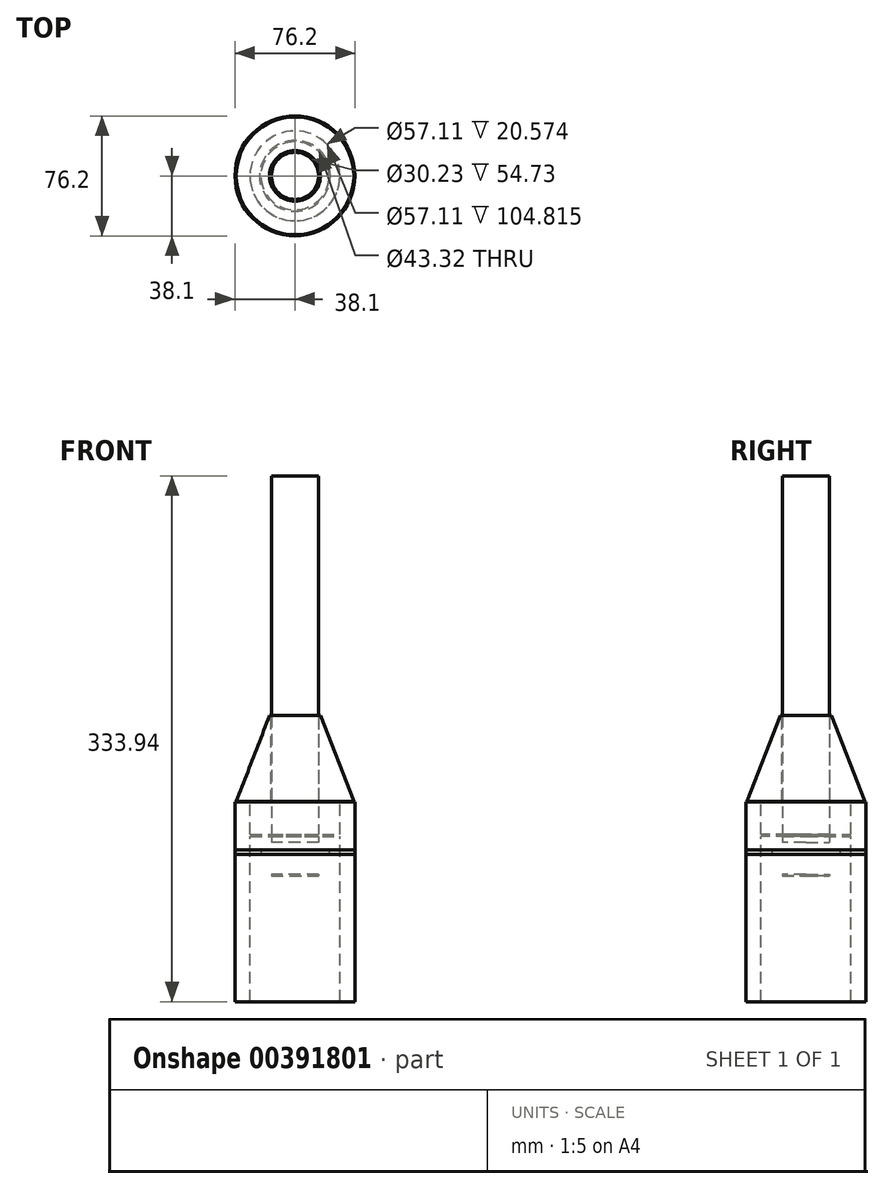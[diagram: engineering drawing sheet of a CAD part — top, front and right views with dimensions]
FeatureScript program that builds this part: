
annotation { "Feature Type Name" : "Feature", "Feature Type Description" : "" }
export const myFeature = defineFeature(function(context is Context, id is Id, definition is map)
    precondition{}
    {
        {
            var Q0;
            Q0=qCreatedBy(makeId("Front.planeOp"),FACE);
            var sketch = newSketch(context, id + "F0", { "sketchPlane" : qUnion([Q0])});
            skLineSegment(sketch, "E0.bottom", {"start": v(0, 67.99) * mm, "end": v(-38.1, 67.99) * mm});
            skLineSegment(sketch, "E0.top", {"start": v(0, -59.01) * mm, "end": v(-38.1, -59.01) * mm});
            skLineSegment(sketch, "E0.left", {"start": v(0, 67.99) * mm, "end": v(0, -59.01) * mm});
            skLineSegment(sketch, "E0.right", {"start": v(-38.1, 67.99) * mm, "end": v(-38.1, -59.01) * mm});
            skSolve(sketch);
        }
        {
            var Q0;
            Q0=makeQuery(id+"F0.imprint","IMPRINT",FACE,{"disambiguationData":[TD([[makeQuery(id+"F0.imprint","IMPRINT",EDGE,{"derivedFrom":sQuery(id+"F0.wireOp",EDGE,"E0.bottom")}),1.0]])]});
            var Q1;
            Q1=sQuery(id+"F0.wireOp",EDGE,"E0.left");
            revolve(context, id + "F1", {"entities" : qUnion([Q0]), "axis" : qUnion([Q1]), "revolveType" : RevolveType.FULL});
        }
        {
            var Q0;
            Q0=qCreatedBy(makeId("Front.planeOp"),FACE);
            var sketch = newSketch(context, id + "F2", { "sketchPlane" : qUnion([Q0])});
            skLineSegment(sketch, "E1", {"start": v(0, 67.85) * mm, "end": v(0, 122.67) * mm});
            skLineSegment(sketch, "E2", {"start": v(0, 122.67) * mm, "end": v(-16.13, 122.67) * mm});
            skLineSegment(sketch, "E3", {"start": v(-16.13, 122.67) * mm, "end": v(-37.35, 68.07) * mm});
            skLineSegment(sketch, "E4", {"start": v(-37.35, 68.07) * mm, "end": v(0, 67.85) * mm});
            skSolve(sketch);
        }
        {
            var Q0;
            Q0=makeQuery(id+"F2.imprint","IMPRINT",FACE,{"disambiguationData":[TD([[makeQuery(id+"F2.imprint","IMPRINT",EDGE,{"derivedFrom":sQuery(id+"F2.wireOp",EDGE,"E1")}),1.0]])]});
            var Q1;
            Q1=sQuery(id+"F2.wireOp",EDGE,"E1");
            revolve(context, id + "F3", {"operationType" : NewBodyOperationType.ADD, "entities" : qUnion([Q0]), "axis" : qUnion([Q1]), "revolveType" : RevolveType.FULL});
        }
        {
            var Q0;
            Q0=qCreatedBy(makeId("Front.planeOp"),FACE);
            var sketch = newSketch(context, id + "F4", { "sketchPlane" : qUnion([Q0])});
            skLineSegment(sketch, "E5.bottom", {"start": v(0, -74.87) * mm, "end": v(-15.11, -74.87) * mm});
            skLineSegment(sketch, "E5.top", {"start": v(0, 135.5) * mm, "end": v(-15.11, 135.5) * mm});
            skLineSegment(sketch, "E5.left", {"start": v(0, -74.87) * mm, "end": v(0, 135.5) * mm});
            skLineSegment(sketch, "E5.right", {"start": v(-15.11, -74.87) * mm, "end": v(-15.11, 135.5) * mm});
            skSolve(sketch);
        }
        {
            var Q0;
            Q0=makeQuery(id+"F4.imprint","IMPRINT",FACE,{"disambiguationData":[TD([[makeQuery(id+"F4.imprint","IMPRINT",EDGE,{"derivedFrom":sQuery(id+"F4.wireOp",EDGE,"E5.bottom")}),-1.0]])]});
            var Q1;
            Q1=sQuery(id+"F4.wireOp",EDGE,"E5.left");
            revolve(context, id + "F5", {"operationType" : NewBodyOperationType.REMOVE, "entities" : qUnion([Q0]), "axis" : qUnion([Q1]), "revolveType" : RevolveType.FULL, "oppositeDirection" : true});
        }
        {
            var Q0;
            Q0=qCreatedBy(makeId("Front.planeOp"),FACE);
            var sketch = newSketch(context, id + "F6", { "sketchPlane" : qUnion([Q0])});
            skLineSegment(sketch, "E6.bottom", {"start": v(0, -70.21) * mm, "end": v(-28.55, -70.21) * mm});
            skLineSegment(sketch, "E6.top", {"start": v(0, 67.94) * mm, "end": v(-28.55, 67.94) * mm});
            skLineSegment(sketch, "E6.left", {"start": v(0, -70.21) * mm, "end": v(0, 67.94) * mm});
            skLineSegment(sketch, "E6.right", {"start": v(-28.55, -70.21) * mm, "end": v(-28.55, 67.94) * mm});
            skSolve(sketch);
        }
        {
            var Q0;
            Q0=makeQuery(id+"F6.imprint","IMPRINT",FACE,{"disambiguationData":[TD([[makeQuery(id+"F6.imprint","IMPRINT",EDGE,{"derivedFrom":sQuery(id+"F6.wireOp",EDGE,"E6.bottom")}),-1.0]])]});
            var Q1;
            Q1=sQuery(id+"F6.wireOp",EDGE,"E6.left");
            revolve(context, id + "F7", {"operationType" : NewBodyOperationType.REMOVE, "entities" : qUnion([Q0]), "axis" : qUnion([Q1]), "revolveType" : RevolveType.FULL, "oppositeDirection" : true});
        }
        {
            var Q0;
            Q0=qCreatedBy(makeId("Front.planeOp"),FACE);
            var sketch = newSketch(context, id + "F8", { "sketchPlane" : qUnion([Q0])});
            skLineSegment(sketch, "E7.bottom", {"start": v(0, 20.93) * mm, "end": v(-15, 20.93) * mm});
            skLineSegment(sketch, "E7.top", {"start": v(0, 274.93) * mm, "end": v(-15, 274.93) * mm});
            skLineSegment(sketch, "E7.left", {"start": v(0, 20.93) * mm, "end": v(0, 274.93) * mm});
            skLineSegment(sketch, "E7.right", {"start": v(-15, 20.93) * mm, "end": v(-15, 274.93) * mm});
            skSolve(sketch);
        }
        {
            var Q0;
            Q0=makeQuery(id+"F8.imprint","IMPRINT",FACE,{"disambiguationData":[TD([[makeQuery(id+"F8.imprint","IMPRINT",EDGE,{"derivedFrom":sQuery(id+"F8.wireOp",EDGE,"E7.bottom")}),-1.0]])]});
            var Q1;
            Q1=sQuery(id+"F8.wireOp",EDGE,"E7.left");
            revolve(context, id + "F9", {"entities" : qUnion([Q0]), "axis" : qUnion([Q1]), "revolveType" : RevolveType.FULL});
        }
        {
            var Q0;
            Q0=qCreatedBy(makeId("Front.planeOp"),FACE);
            var sketch = newSketch(context, id + "F10", { "sketchPlane" : qUnion([Q0])});
            skLineSegment(sketch, "E8", {"start": v(0, 125.98) * mm, "end": v(0, 141.22) * mm});
            skLineSegment(sketch, "E9", {"start": v(0, 141.22) * mm, "end": v(-1.06, 141.22) * mm});
            skLineSegment(sketch, "E10", {"start": v(-1.06, 141.22) * mm, "end": v(-14.71, 125.86) * mm});
            skLineSegment(sketch, "E11", {"start": v(-14.71, 125.86) * mm, "end": v(0, 125.98) * mm});
            skSolve(sketch);
        }
        {
            var Q0;
            Q0=makeQuery(id+"F10.imprint","IMPRINT",FACE,{"disambiguationData":[TD([[makeQuery(id+"F10.imprint","IMPRINT",EDGE,{"derivedFrom":sQuery(id+"F10.wireOp",EDGE,"E8")}),1.0]])]});
            var Q1;
            Q1=sQuery(id+"F10.wireOp",EDGE,"E8");
            revolve(context, id + "F11", {"operationType" : NewBodyOperationType.ADD, "entities" : qUnion([Q0]), "axis" : qUnion([Q1]), "revolveType" : RevolveType.FULL});
        }
        {
            var Q0;
            Q0=qCreatedBy(makeId("Front.planeOp"),FACE);
            var sketch = newSketch(context, id + "F12", { "sketchPlane" : qUnion([Q0])});
            skLineSegment(sketch, "E12.bottom", {"start": v(0, 45.8) * mm, "end": v(-29.44, 45.8) * mm});
            skLineSegment(sketch, "E12.top", {"start": v(0, 47.36) * mm, "end": v(-29.44, 47.36) * mm});
            skLineSegment(sketch, "E12.left", {"start": v(0, 45.8) * mm, "end": v(0, 47.36) * mm});
            skLineSegment(sketch, "E12.right", {"start": v(-29.44, 45.8) * mm, "end": v(-29.44, 47.36) * mm});
            skSolve(sketch);
        }
        {
            var Q0;
            Q0=makeQuery(id+"F12.imprint","IMPRINT",FACE,{"disambiguationData":[TD([[makeQuery(id+"F12.imprint","IMPRINT",EDGE,{"derivedFrom":sQuery(id+"F12.wireOp",EDGE,"E12.bottom")}),-1.0]])]});
            var Q1;
            Q1=sQuery(id+"F12.wireOp",EDGE,"E12.left");
            revolve(context, id + "F13", {"operationType" : NewBodyOperationType.ADD, "entities" : qUnion([Q0]), "axis" : qUnion([Q1]), "revolveType" : RevolveType.FULL});
        }
        {
            var Q0;
            Q0=qCreatedBy(makeId("Front.planeOp"),FACE);
            var sketch = newSketch(context, id + "F14", { "sketchPlane" : qUnion([Q0])});
            skLineSegment(sketch, "E13.bottom", {"start": v(0, 34.52) * mm, "end": v(-38.1, 34.52) * mm});
            skLineSegment(sketch, "E13.top", {"start": v(0, 37.34) * mm, "end": v(-38.1, 37.34) * mm});
            skLineSegment(sketch, "E13.left", {"start": v(0, 34.52) * mm, "end": v(0, 37.34) * mm});
            skLineSegment(sketch, "E13.right", {"start": v(-38.1, 34.52) * mm, "end": v(-38.1, 37.34) * mm});
            skSolve(sketch);
        }
        {
            var Q0;
            Q0=makeQuery(id+"F14.imprint","IMPRINT",FACE,{"disambiguationData":[TD([[makeQuery(id+"F14.imprint","IMPRINT",EDGE,{"derivedFrom":sQuery(id+"F14.wireOp",EDGE,"E13.bottom")}),-1.0]])]});
            var Q1;
            Q1=sQuery(id+"F14.wireOp",EDGE,"E13.left");
            revolve(context, id + "F15", {"entities" : qUnion([Q0]), "axis" : qUnion([Q1]), "revolveType" : RevolveType.FULL});
        }
        {
            var Q0;
            Q0=qCreatedBy(makeId("Front.planeOp"),FACE);
            var sketch = newSketch(context, id + "F16", { "sketchPlane" : qUnion([Q0])});
            skLineSegment(sketch, "E14.bottom", {"start": v(-21.66, 42.22) * mm, "end": v(0, 42.22) * mm});
            skLineSegment(sketch, "E14.top", {"start": v(-21.66, 21.88) * mm, "end": v(0, 21.88) * mm});
            skLineSegment(sketch, "E14.left", {"start": v(-21.66, 42.22) * mm, "end": v(-21.66, 21.88) * mm});
            skLineSegment(sketch, "E14.right", {"start": v(0, 42.22) * mm, "end": v(0, 21.88) * mm});
            skSolve(sketch);
        }
        {
            var Q0;
            Q0=makeQuery(id+"F16.imprint","IMPRINT",FACE,{"disambiguationData":[TD([[makeQuery(id+"F16.imprint","IMPRINT",EDGE,{"derivedFrom":sQuery(id+"F16.wireOp",EDGE,"E14.bottom")}),-1.0]])]});
            var Q1;
            Q1=sQuery(id+"F16.wireOp",EDGE,"E14.right");
            revolve(context, id + "F17", {"operationType" : NewBodyOperationType.REMOVE, "entities" : qUnion([Q0]), "axis" : qUnion([Q1]), "revolveType" : RevolveType.FULL, "oppositeDirection" : true});
        }
    });
